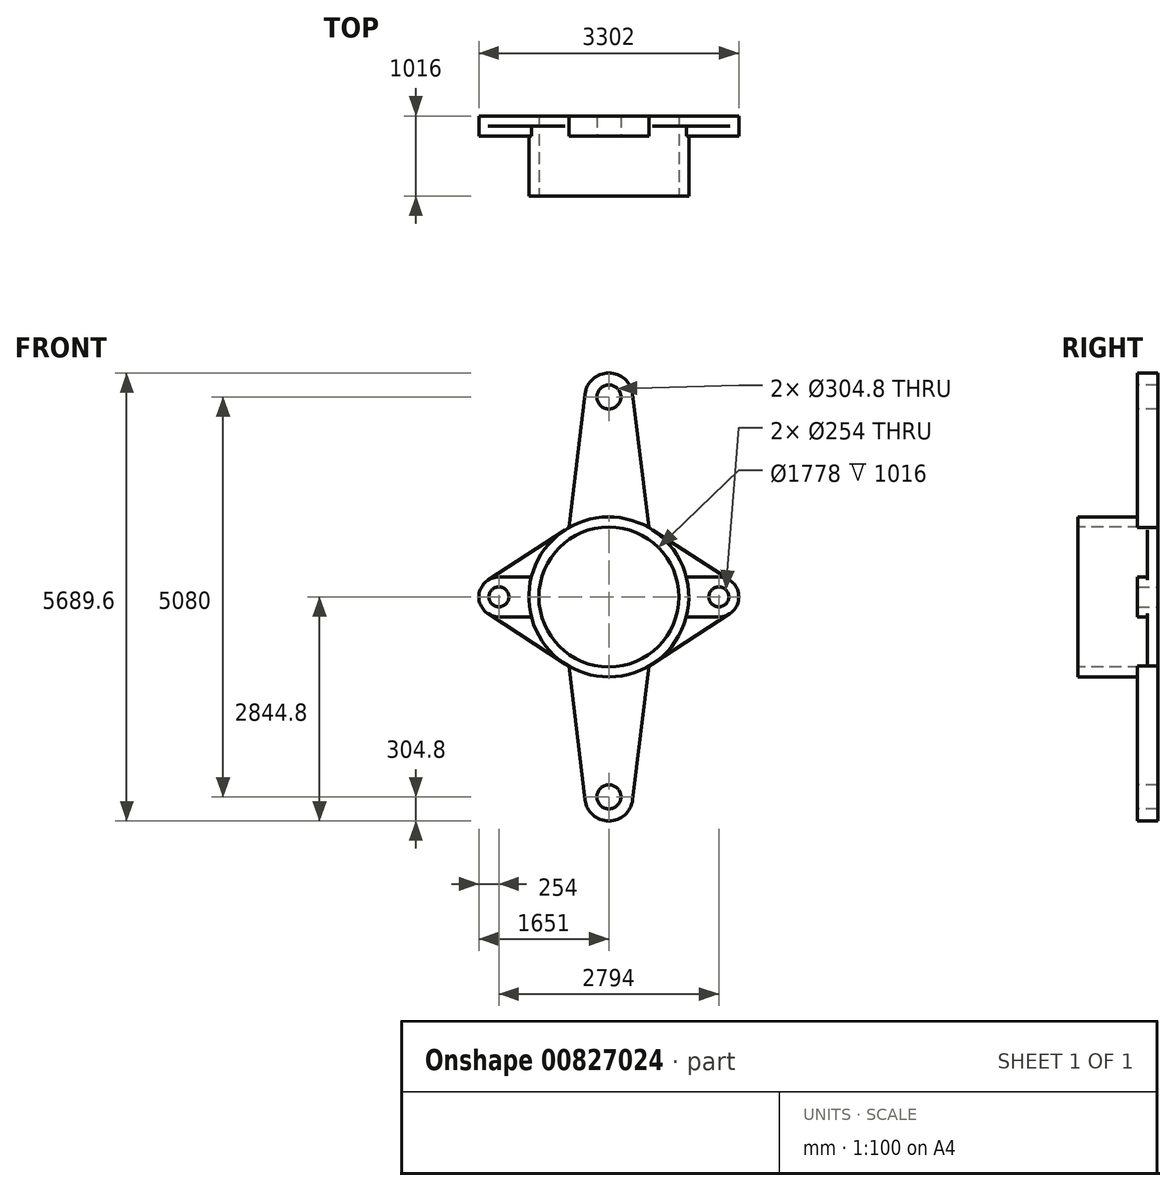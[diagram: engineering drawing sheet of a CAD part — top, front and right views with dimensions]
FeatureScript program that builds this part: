
annotation { "Feature Type Name" : "Feature", "Feature Type Description" : "" }
export const myFeature = defineFeature(function(context is Context, id is Id, definition is map)
    precondition{}
    {
        {
            var Q0;
            Q0=qCreatedBy(makeId("Front.planeOp"),FACE);
            var sketch = newSketch(context, id + "F0", { "sketchPlane" : qUnion([Q0])});
            skCircle(sketch, "E0", {"center": v(0, 0) * mm, "radius": 1016 * mm});
            skSolve(sketch);
        }
        {
            var Q0;
            Q0 = qSketchRegion(id + "F0", true);
            extrude(context, id + "F1", {"entities" : qUnion([Q0]), "depth" : 1016 * mm, "offsetDistance" : 25.4 * mm});
        }
        {
            var Q0;
            Q0=qCreatedBy(makeId("Front.planeOp"),FACE);
            var sketch = newSketch(context, id + "F2", { "sketchPlane" : qUnion([Q0])});
            skLineSegment(sketch, "E1", {"start": v(0, 2540) * mm, "end": v(0, -2540) * mm, "construction": true});
            skArc(sketch, "E2", {"start": v(302.6, 2576.63) * mm, "mid": v(0, 2844.8) * mm, "end": v(-302.6, 2576.63) * mm});
            skLineSegment(sketch, "E3", {"start": v(-508, 879.88) * mm, "end": v(-302.6, 2576.63) * mm});
            skLineSegment(sketch, "E4", {"start": v(302.6, 2576.63) * mm, "end": v(508, 879.88) * mm});
            skLineSegment(sketch, "E5", {"start": v(-508, 879.88) * mm, "end": v(508, 879.88) * mm});
            skSolve(sketch);
        }
        {
            var Q0;
            Q0 = qSketchRegion(id + "F2", true);
            extrude(context, id + "F3", {"entities" : qUnion([Q0]), "operationType" : NewBodyOperationType.ADD, "depth" : 254 * mm, "offsetDistance" : 25.4 * mm});
        }
        {
            var Q0;
            Q0=makeQuery(id+"F3.opExtrude","CAP_FACE",FACE,{"disambiguationData":[OSD([sQuery(id+"F2.wireOp",EDGE,"E2"),sQuery(id+"F2.wireOp",EDGE,"E3"),sQuery(id+"F2.wireOp",EDGE,"E4"),sQuery(id+"F2.wireOp",EDGE,"E5")])],"isStart":false});
            var sketch = newSketch(context, id + "F4", { "sketchPlane" : qUnion([Q0])});
            skLineSegment(sketch, "E6", {"start": v(0, 2540) * mm, "end": v(0, -2540) * mm, "construction": true});
            skCircle(sketch, "E7", {"center": v(0, 2540) * mm, "radius": 152.4 * mm});
            skSolve(sketch);
        }
        {
            var Q0;
            Q0 = qSketchRegion(id + "F4", true);
            extrude(context, id + "F5", {"entities" : qUnion([Q0]), "operationType" : NewBodyOperationType.REMOVE, "endBound" : BoundingType.THROUGH_ALL, "oppositeDirection" : true, "depth" : 25.4 * mm, "offsetDistance" : 25.4 * mm});
        }
        {
            var Q0;
            Q0=makeQuery(id+"F1.opExtrude","SWEPT_BODY",BODY,{"disambiguationData":[OSD([sQuery(id+"F0.wireOp",EDGE,"E0")])]});
            var Q1;
            Q1=qCreatedBy(makeId("Top.planeOp"),FACE);
            mirror(context, id + "F6", {"operationType" : NewBodyOperationType.ADD, "entities" : qUnion([Q0]), "mirrorPlane" : qUnion([Q1])});
        }
        {
            var Q0;
            Q0=qCreatedBy(makeId("Front.planeOp"),FACE);
            var sketch = newSketch(context, id + "F7", { "sketchPlane" : qUnion([Q0])});
            skLineSegment(sketch, "E8", {"start": v(-1397, 0) * mm, "end": v(1397, 0) * mm, "construction": true});
            skCircle(sketch, "E9", {"center": v(1397, 0) * mm, "radius": 127 * mm});
            skArc(sketch, "E10", {"start": v(1397, -254) * mm, "mid": v(1651, 0) * mm, "end": v(1397, 254) * mm});
            skLineSegment(sketch, "E11", {"start": v(1397, 254) * mm, "end": v(983.74, 254) * mm});
            skLineSegment(sketch, "E12", {"start": v(1397, -254) * mm, "end": v(983.74, -254) * mm});
            skLineSegment(sketch, "E13", {"start": v(983.74, 254) * mm, "end": v(983.74, -254) * mm});
            skSolve(sketch);
        }
        {
            var Q0;
            Q0 = qSketchRegion(id + "F7", true);
            extrude(context, id + "F8", {"entities" : qUnion([Q0]), "operationType" : NewBodyOperationType.ADD, "depth" : 254 * mm, "offsetDistance" : 25.4 * mm});
        }
        {
            var Q0;
            Q0=qCreatedBy(makeId("Front.planeOp"),FACE);
            var sketch = newSketch(context, id + "F9", { "sketchPlane" : qUnion([Q0])});
            skLineSegment(sketch, "E14", {"start": v(554.18, 851.55) * mm, "end": v(1535.55, 212.89) * mm});
            skLineSegment(sketch, "E15", {"start": v(554.18, -851.55) * mm, "end": v(1535.55, -212.89) * mm});
            skLineSegment(sketch, "E16", {"start": v(554.18, 851.55) * mm, "end": v(554.18, -851.55) * mm});
            skLineSegment(sketch, "E17", {"start": v(1535.55, 212.89) * mm, "end": v(1535.55, -212.89) * mm});
            skSolve(sketch);
        }
        {
            var Q0;
            Q0 = qSketchRegion(id + "F9", true);
            extrude(context, id + "F10", {"entities" : qUnion([Q0]), "operationType" : NewBodyOperationType.ADD, "depth" : 127 * mm, "offsetDistance" : 25.4 * mm});
        }
        {
            var Q0;
            Q0=makeQuery(id+"F10.boolean.opBoolean","SPLIT",FACE,{"disambiguationData":[TD([makeQuery(id+"F8.opExtrude","SWEPT_FACE",FACE,{"disambiguationData":[OSD([sQuery(id+"F7.wireOp",EDGE,"E9")])]})])],"derivedFrom":makeQuery(id+"F10.opExtrude","CAP_FACE",FACE,{"disambiguationData":[OSD([sQuery(id+"F9.wireOp",EDGE,"E14"),sQuery(id+"F9.wireOp",EDGE,"E15"),sQuery(id+"F9.wireOp",EDGE,"E16"),sQuery(id+"F9.wireOp",EDGE,"E17")])],"isStart":false})});
            var sketch = newSketch(context, id + "F11", { "sketchPlane" : qUnion([Q0])});
            skCircle(sketch, "E18", {"center": v(1397, 0) * mm, "radius": 127 * mm});
            skSolve(sketch);
        }
        {
            var Q0;
            Q0=makeQuery(id+"F11.imprint","IMPRINT",FACE,{"disambiguationData":[TD([[makeQuery(id+"F11.imprint","IMPRINT",EDGE,{"derivedFrom":sQuery(id+"F11.wireOp",EDGE,"E18")}),1.0]])]});
            extrude(context, id + "F12", {"entities" : qUnion([Q0]), "operationType" : NewBodyOperationType.REMOVE, "endBound" : BoundingType.THROUGH_ALL, "oppositeDirection" : true, "depth" : 25.4 * mm, "offsetDistance" : 25.4 * mm});
        }
        {
            var Q0;
            Q0=makeQuery(id+"F1.opExtrude","SWEPT_BODY",BODY,{"disambiguationData":[OSD([sQuery(id+"F0.wireOp",EDGE,"E0")])]});
            var Q1;
            Q1=qCreatedBy(makeId("Right.planeOp"),FACE);
            mirror(context, id + "F13", {"operationType" : NewBodyOperationType.ADD, "entities" : qUnion([Q0]), "mirrorPlane" : qUnion([Q1])});
        }
        {
            var Q0;
            Q0=makeQuery(id+"F1.opExtrude","CAP_FACE",FACE,{"disambiguationData":[OSD([sQuery(id+"F0.wireOp",EDGE,"E0")])],"isStart":false});
            var sketch = newSketch(context, id + "F14", { "sketchPlane" : qUnion([Q0])});
            skCircle(sketch, "E19", {"center": v(0, 0) * mm, "radius": 889 * mm});
            skSolve(sketch);
        }
        {
            var Q0;
            Q0 = qSketchRegion(id + "F14", true);
            extrude(context, id + "F15", {"entities" : qUnion([Q0]), "operationType" : NewBodyOperationType.REMOVE, "endBound" : BoundingType.THROUGH_ALL, "oppositeDirection" : true, "depth" : 25.4 * mm, "offsetDistance" : 25.4 * mm});
        }
    });
